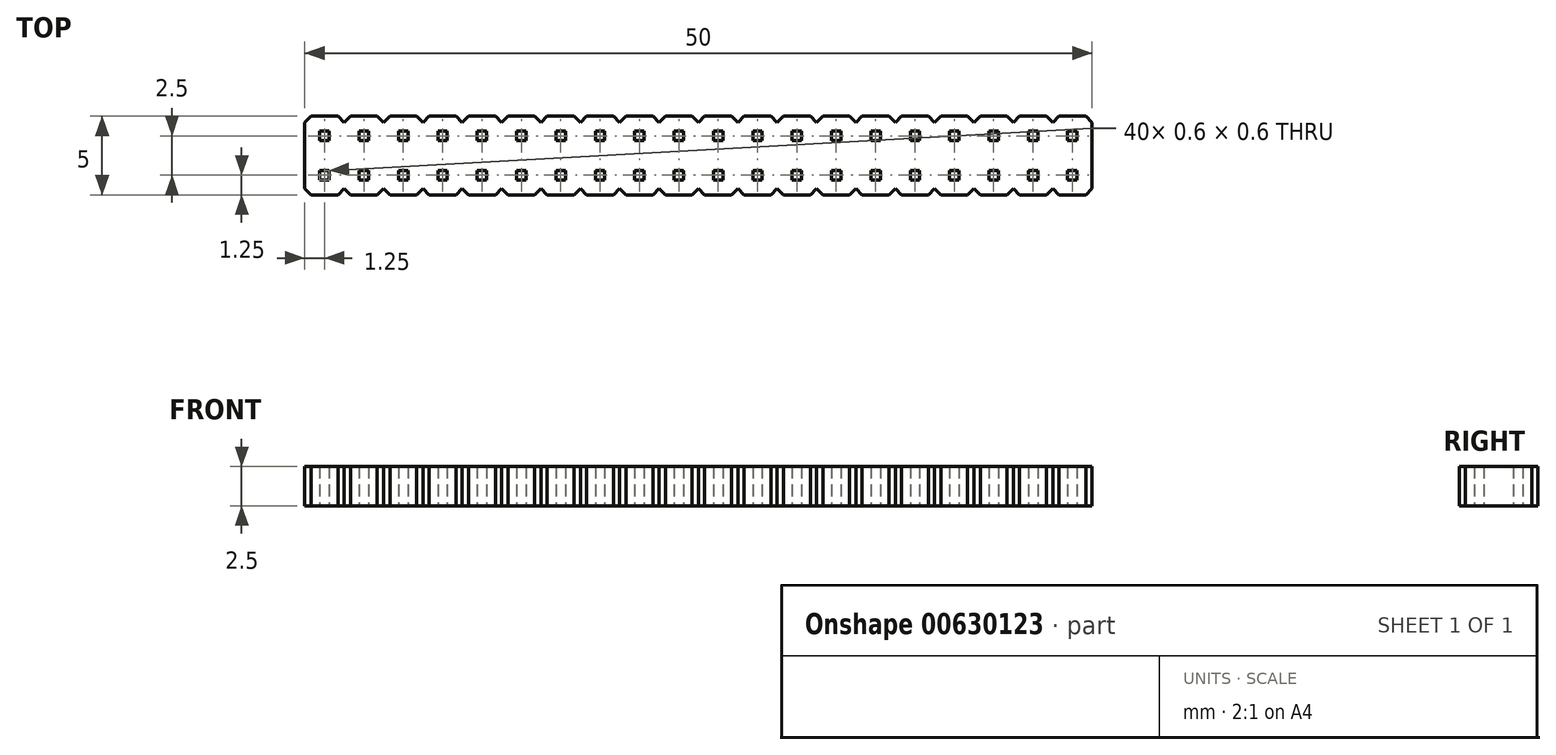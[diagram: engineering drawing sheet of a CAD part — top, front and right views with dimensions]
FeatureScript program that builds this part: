
annotation { "Feature Type Name" : "Feature", "Feature Type Description" : "" }
export const myFeature = defineFeature(function(context is Context, id is Id, definition is map)
    precondition{}
    {
        {
            var Q0;
            Q0=qCreatedBy(makeId("Top.planeOp"),FACE);
            var sketch = newSketch(context, id + "F0", { "sketchPlane" : qUnion([Q0])});
            skLineSegment(sketch, "E0.bottom", {"start": v(0.4, 0) * mm, "end": v(2.1, 0) * mm});
            skLineSegment(sketch, "E0.top", {"start": v(0.4, 5) * mm, "end": v(2.1, 5) * mm});
            skLineSegment(sketch, "E0.left", {"start": v(0, 0.4) * mm, "end": v(0, 4.6) * mm});
            skLineSegment(sketch, "E0.right", {"start": v(50, 0.4) * mm, "end": v(50, 4.6) * mm});
            skLineSegment(sketch, "E1", {"start": v(25, 5) * mm, "end": v(25, 0) * mm, "construction": true});
            skLineSegment(sketch, "E2", {"start": v(0, 2.5) * mm, "end": v(50, 2.5) * mm, "construction": true});
            skLineSegment(sketch, "E3.bottom", {"start": v(0.95, 4.05) * mm, "end": v(1.55, 4.05) * mm});
            skLineSegment(sketch, "E3.top", {"start": v(0.95, 3.45) * mm, "end": v(1.55, 3.45) * mm});
            skLineSegment(sketch, "E3.left", {"start": v(0.95, 4.05) * mm, "end": v(0.95, 3.45) * mm});
            skLineSegment(sketch, "E3.right", {"start": v(1.55, 4.05) * mm, "end": v(1.55, 3.45) * mm});
            skLineSegment(sketch, "E4", {"start": v(0, 4.6) * mm, "end": v(0.4, 5) * mm});
            skLineSegment(sketch, "E5", {"start": v(2.5, 5) * mm, "end": v(2.5, 2.5) * mm, "construction": true});
            skLineSegment(sketch, "E6", {"start": v(2.1, 5) * mm, "end": v(2.5, 4.6) * mm});
            skLineSegment(sketch, "E7.1.0.0", {"start": v(3.45, 3.45) * mm, "end": v(4.05, 3.45) * mm});
            skLineSegment(sketch, "E7.1.0.1", {"start": v(3.45, 4.05) * mm, "end": v(3.45, 3.45) * mm});
            skLineSegment(sketch, "E7.1.0.2", {"start": v(4.05, 4.05) * mm, "end": v(4.05, 3.45) * mm});
            skLineSegment(sketch, "E7.1.0.3", {"start": v(3.45, 4.05) * mm, "end": v(4.05, 4.05) * mm});
            skLineSegment(sketch, "E7.1.0.4", {"start": v(2.5, 4.6) * mm, "end": v(2.9, 5) * mm});
            skLineSegment(sketch, "E7.1.0.5", {"start": v(4.6, 5) * mm, "end": v(5, 4.6) * mm});
            skLineSegment(sketch, "E7.2.0.0", {"start": v(5.95, 3.45) * mm, "end": v(6.55, 3.45) * mm});
            skLineSegment(sketch, "E7.2.0.1", {"start": v(5.95, 4.05) * mm, "end": v(5.95, 3.45) * mm});
            skLineSegment(sketch, "E7.2.0.2", {"start": v(6.55, 4.05) * mm, "end": v(6.55, 3.45) * mm});
            skLineSegment(sketch, "E7.2.0.3", {"start": v(5.95, 4.05) * mm, "end": v(6.55, 4.05) * mm});
            skLineSegment(sketch, "E7.2.0.4", {"start": v(5, 4.6) * mm, "end": v(5.4, 5) * mm});
            skLineSegment(sketch, "E7.2.0.5", {"start": v(7.1, 5) * mm, "end": v(7.5, 4.6) * mm});
            skLineSegment(sketch, "E7.3.0.0", {"start": v(8.45, 3.45) * mm, "end": v(9.05, 3.45) * mm});
            skLineSegment(sketch, "E7.3.0.1", {"start": v(8.45, 4.05) * mm, "end": v(8.45, 3.45) * mm});
            skLineSegment(sketch, "E7.3.0.2", {"start": v(9.05, 4.05) * mm, "end": v(9.05, 3.45) * mm});
            skLineSegment(sketch, "E7.3.0.3", {"start": v(8.45, 4.05) * mm, "end": v(9.05, 4.05) * mm});
            skLineSegment(sketch, "E7.3.0.4", {"start": v(7.5, 4.6) * mm, "end": v(7.9, 5) * mm});
            skLineSegment(sketch, "E7.3.0.5", {"start": v(9.6, 5) * mm, "end": v(10, 4.6) * mm});
            skLineSegment(sketch, "E7.4.0.0", {"start": v(10.95, 3.45) * mm, "end": v(11.55, 3.45) * mm});
            skLineSegment(sketch, "E7.4.0.1", {"start": v(10.95, 4.05) * mm, "end": v(10.95, 3.45) * mm});
            skLineSegment(sketch, "E7.4.0.2", {"start": v(11.55, 4.05) * mm, "end": v(11.55, 3.45) * mm});
            skLineSegment(sketch, "E7.4.0.3", {"start": v(10.95, 4.05) * mm, "end": v(11.55, 4.05) * mm});
            skLineSegment(sketch, "E7.4.0.4", {"start": v(10, 4.6) * mm, "end": v(10.4, 5) * mm});
            skLineSegment(sketch, "E7.4.0.5", {"start": v(12.1, 5) * mm, "end": v(12.5, 4.6) * mm});
            skLineSegment(sketch, "E7.5.0.0", {"start": v(13.45, 3.45) * mm, "end": v(14.05, 3.45) * mm});
            skLineSegment(sketch, "E7.5.0.1", {"start": v(13.45, 4.05) * mm, "end": v(13.45, 3.45) * mm});
            skLineSegment(sketch, "E7.5.0.2", {"start": v(14.05, 4.05) * mm, "end": v(14.05, 3.45) * mm});
            skLineSegment(sketch, "E7.5.0.3", {"start": v(13.45, 4.05) * mm, "end": v(14.05, 4.05) * mm});
            skLineSegment(sketch, "E7.5.0.4", {"start": v(12.5, 4.6) * mm, "end": v(12.9, 5) * mm});
            skLineSegment(sketch, "E7.5.0.5", {"start": v(14.6, 5) * mm, "end": v(15, 4.6) * mm});
            skLineSegment(sketch, "E7.6.0.0", {"start": v(15.95, 3.45) * mm, "end": v(16.55, 3.45) * mm});
            skLineSegment(sketch, "E7.6.0.1", {"start": v(15.95, 4.05) * mm, "end": v(15.95, 3.45) * mm});
            skLineSegment(sketch, "E7.6.0.2", {"start": v(16.55, 4.05) * mm, "end": v(16.55, 3.45) * mm});
            skLineSegment(sketch, "E7.6.0.3", {"start": v(15.95, 4.05) * mm, "end": v(16.55, 4.05) * mm});
            skLineSegment(sketch, "E7.6.0.4", {"start": v(15, 4.6) * mm, "end": v(15.4, 5) * mm});
            skLineSegment(sketch, "E7.6.0.5", {"start": v(17.1, 5) * mm, "end": v(17.5, 4.6) * mm});
            skLineSegment(sketch, "E7.7.0.0", {"start": v(18.45, 3.45) * mm, "end": v(19.05, 3.45) * mm});
            skLineSegment(sketch, "E7.7.0.1", {"start": v(18.45, 4.05) * mm, "end": v(18.45, 3.45) * mm});
            skLineSegment(sketch, "E7.7.0.2", {"start": v(19.05, 4.05) * mm, "end": v(19.05, 3.45) * mm});
            skLineSegment(sketch, "E7.7.0.3", {"start": v(18.45, 4.05) * mm, "end": v(19.05, 4.05) * mm});
            skLineSegment(sketch, "E7.7.0.4", {"start": v(17.5, 4.6) * mm, "end": v(17.9, 5) * mm});
            skLineSegment(sketch, "E7.7.0.5", {"start": v(19.6, 5) * mm, "end": v(20, 4.6) * mm});
            skLineSegment(sketch, "E7.8.0.0", {"start": v(20.95, 3.45) * mm, "end": v(21.55, 3.45) * mm});
            skLineSegment(sketch, "E7.8.0.1", {"start": v(20.95, 4.05) * mm, "end": v(20.95, 3.45) * mm});
            skLineSegment(sketch, "E7.8.0.2", {"start": v(21.55, 4.05) * mm, "end": v(21.55, 3.45) * mm});
            skLineSegment(sketch, "E7.8.0.3", {"start": v(20.95, 4.05) * mm, "end": v(21.55, 4.05) * mm});
            skLineSegment(sketch, "E7.8.0.4", {"start": v(20, 4.6) * mm, "end": v(20.4, 5) * mm});
            skLineSegment(sketch, "E7.8.0.5", {"start": v(22.1, 5) * mm, "end": v(22.5, 4.6) * mm});
            skLineSegment(sketch, "E7.9.0.0", {"start": v(23.45, 3.45) * mm, "end": v(24.05, 3.45) * mm});
            skLineSegment(sketch, "E7.9.0.1", {"start": v(23.45, 4.05) * mm, "end": v(23.45, 3.45) * mm});
            skLineSegment(sketch, "E7.9.0.2", {"start": v(24.05, 4.05) * mm, "end": v(24.05, 3.45) * mm});
            skLineSegment(sketch, "E7.9.0.3", {"start": v(23.45, 4.05) * mm, "end": v(24.05, 4.05) * mm});
            skLineSegment(sketch, "E7.9.0.4", {"start": v(22.5, 4.6) * mm, "end": v(22.9, 5) * mm});
            skLineSegment(sketch, "E7.9.0.5", {"start": v(24.6, 5) * mm, "end": v(25, 4.6) * mm});
            skLineSegment(sketch, "E7.direction1", {"start": v(0.95, 3.45) * mm, "end": v(3.45, 3.45) * mm, "construction": true});
            skLineSegment(sketch, "E8.MirrorCS", {"start": v(23.45, 0.95) * mm, "end": v(24.05, 0.95) * mm});
            skLineSegment(sketch, "E9.MirrorCS", {"start": v(20.95, 1.55) * mm, "end": v(21.55, 1.55) * mm});
            skLineSegment(sketch, "E10.MirrorCS", {"start": v(23.45, 1.55) * mm, "end": v(24.05, 1.55) * mm});
            skLineSegment(sketch, "E11.MirrorCS", {"start": v(20.95, 0.95) * mm, "end": v(21.55, 0.95) * mm});
            skLineSegment(sketch, "E12.MirrorCS", {"start": v(0.95, 1.55) * mm, "end": v(1.55, 1.55) * mm});
            skLineSegment(sketch, "E13.MirrorCS", {"start": v(10.95, 0.95) * mm, "end": v(11.55, 0.95) * mm});
            skLineSegment(sketch, "E14.MirrorCS", {"start": v(18.45, 0.95) * mm, "end": v(18.45, 1.55) * mm});
            skLineSegment(sketch, "E15.MirrorCS", {"start": v(8.45, 1.55) * mm, "end": v(9.05, 1.55) * mm});
            skLineSegment(sketch, "E16.MirrorCS", {"start": v(21.55, 0.95) * mm, "end": v(21.55, 1.55) * mm});
            skLineSegment(sketch, "E17.MirrorCS", {"start": v(11.55, 0.95) * mm, "end": v(11.55, 1.55) * mm});
            skLineSegment(sketch, "E18.MirrorCS", {"start": v(18.45, 1.55) * mm, "end": v(19.05, 1.55) * mm});
            skLineSegment(sketch, "E19.MirrorCS", {"start": v(13.45, 0.95) * mm, "end": v(14.05, 0.95) * mm});
            skLineSegment(sketch, "E20.MirrorCS", {"start": v(20.95, 0.95) * mm, "end": v(20.95, 1.55) * mm});
            skLineSegment(sketch, "E21.MirrorCS", {"start": v(10.95, 0.95) * mm, "end": v(10.95, 1.55) * mm});
            skLineSegment(sketch, "E22.MirrorCS", {"start": v(3.45, 0.95) * mm, "end": v(4.05, 0.95) * mm});
            skLineSegment(sketch, "E23.MirrorCS", {"start": v(14.05, 0.95) * mm, "end": v(14.05, 1.55) * mm});
            skLineSegment(sketch, "E24.MirrorCS", {"start": v(1.55, 0.95) * mm, "end": v(1.55, 1.55) * mm});
            skLineSegment(sketch, "E25.MirrorCS", {"start": v(0.95, 0.95) * mm, "end": v(0.95, 1.55) * mm});
            skLineSegment(sketch, "E26.MirrorCS", {"start": v(0.95, 0.95) * mm, "end": v(1.55, 0.95) * mm});
            skLineSegment(sketch, "E27.MirrorCS", {"start": v(4.05, 0.95) * mm, "end": v(4.05, 1.55) * mm});
            skLineSegment(sketch, "E28.MirrorCS", {"start": v(3.45, 0.95) * mm, "end": v(3.45, 1.55) * mm});
            skLineSegment(sketch, "E29.MirrorCS", {"start": v(3.45, 1.55) * mm, "end": v(4.05, 1.55) * mm});
            skLineSegment(sketch, "E30.MirrorCS", {"start": v(13.45, 0.95) * mm, "end": v(13.45, 1.55) * mm});
            skLineSegment(sketch, "E31.MirrorCS", {"start": v(10.95, 1.55) * mm, "end": v(11.55, 1.55) * mm});
            skLineSegment(sketch, "E32.MirrorCS", {"start": v(24.05, 0.95) * mm, "end": v(24.05, 1.55) * mm});
            skLineSegment(sketch, "E33.MirrorCS", {"start": v(5.95, 0.95) * mm, "end": v(6.55, 0.95) * mm});
            skLineSegment(sketch, "E34.MirrorCS", {"start": v(13.45, 1.55) * mm, "end": v(14.05, 1.55) * mm});
            skLineSegment(sketch, "E35.MirrorCS", {"start": v(15.95, 0.95) * mm, "end": v(16.55, 0.95) * mm});
            skLineSegment(sketch, "E36.MirrorCS", {"start": v(23.45, 0.95) * mm, "end": v(23.45, 1.55) * mm});
            skLineSegment(sketch, "E37.MirrorCS", {"start": v(6.55, 0.95) * mm, "end": v(6.55, 1.55) * mm});
            skLineSegment(sketch, "E38.MirrorCS", {"start": v(8.45, 0.95) * mm, "end": v(9.05, 0.95) * mm});
            skLineSegment(sketch, "E39.MirrorCS", {"start": v(15.95, 0.95) * mm, "end": v(15.95, 1.55) * mm});
            skLineSegment(sketch, "E40.MirrorCS", {"start": v(18.45, 0.95) * mm, "end": v(19.05, 0.95) * mm});
            skLineSegment(sketch, "E41.MirrorCS", {"start": v(16.55, 0.95) * mm, "end": v(16.55, 1.55) * mm});
            skLineSegment(sketch, "E42.MirrorCS", {"start": v(15.95, 1.55) * mm, "end": v(16.55, 1.55) * mm});
            skLineSegment(sketch, "E43.MirrorCS", {"start": v(9.05, 0.95) * mm, "end": v(9.05, 1.55) * mm});
            skLineSegment(sketch, "E44.MirrorCS", {"start": v(5.95, 0.95) * mm, "end": v(5.95, 1.55) * mm});
            skLineSegment(sketch, "E45.MirrorCS", {"start": v(19.05, 0.95) * mm, "end": v(19.05, 1.55) * mm});
            skLineSegment(sketch, "E46.MirrorCS", {"start": v(8.45, 0.95) * mm, "end": v(8.45, 1.55) * mm});
            skLineSegment(sketch, "E47.MirrorCS", {"start": v(5.95, 1.55) * mm, "end": v(6.55, 1.55) * mm});
            skLineSegment(sketch, "E48.MirrorCS", {"start": v(0.95, 1.55) * mm, "end": v(3.45, 1.55) * mm, "construction": true});
            skLineSegment(sketch, "E49.MirrorCS", {"start": v(0, 0.4) * mm, "end": v(0.4, 0) * mm});
            skLineSegment(sketch, "E50.MirrorCS", {"start": v(2.1, 0) * mm, "end": v(2.5, 0.4) * mm});
            skLineSegment(sketch, "E51.MirrorCS", {"start": v(2.5, 0.4) * mm, "end": v(2.9, 0) * mm});
            skLineSegment(sketch, "E52.MirrorCS", {"start": v(4.6, 0) * mm, "end": v(5, 0.4) * mm});
            skLineSegment(sketch, "E53.MirrorCS", {"start": v(5, 0.4) * mm, "end": v(5.4, 0) * mm});
            skLineSegment(sketch, "E54.MirrorCS", {"start": v(7.1, 0) * mm, "end": v(7.5, 0.4) * mm});
            skLineSegment(sketch, "E55.MirrorCS", {"start": v(7.5, 0.4) * mm, "end": v(7.9, 0) * mm});
            skLineSegment(sketch, "E56.MirrorCS", {"start": v(9.6, 0) * mm, "end": v(10, 0.4) * mm});
            skLineSegment(sketch, "E57.MirrorCS", {"start": v(10, 0.4) * mm, "end": v(10.4, 0) * mm});
            skLineSegment(sketch, "E58.MirrorCS", {"start": v(12.1, 0) * mm, "end": v(12.5, 0.4) * mm});
            skLineSegment(sketch, "E59.MirrorCS", {"start": v(12.5, 0.4) * mm, "end": v(12.9, 0) * mm});
            skLineSegment(sketch, "E60.MirrorCS", {"start": v(14.6, 0) * mm, "end": v(15, 0.4) * mm});
            skLineSegment(sketch, "E61.MirrorCS", {"start": v(15, 0.4) * mm, "end": v(15.4, 0) * mm});
            skLineSegment(sketch, "E62.MirrorCS", {"start": v(17.1, 0) * mm, "end": v(17.5, 0.4) * mm});
            skLineSegment(sketch, "E63.MirrorCS", {"start": v(17.5, 0.4) * mm, "end": v(17.9, 0) * mm});
            skLineSegment(sketch, "E64.MirrorCS", {"start": v(19.6, 0) * mm, "end": v(20, 0.4) * mm});
            skLineSegment(sketch, "E65.MirrorCS", {"start": v(20, 0.4) * mm, "end": v(20.4, 0) * mm});
            skLineSegment(sketch, "E66.MirrorCS", {"start": v(22.1, 0) * mm, "end": v(22.5, 0.4) * mm});
            skLineSegment(sketch, "E67.MirrorCS", {"start": v(22.5, 0.4) * mm, "end": v(22.9, 0) * mm});
            skLineSegment(sketch, "E68.MirrorCS", {"start": v(24.6, 0) * mm, "end": v(25, 0.4) * mm});
            skLineSegment(sketch, "E69.MirrorCS", {"start": v(49.05, 1.55) * mm, "end": v(48.45, 1.55) * mm});
            skLineSegment(sketch, "E70.MirrorCS", {"start": v(49.05, 3.45) * mm, "end": v(48.45, 3.45) * mm});
            skLineSegment(sketch, "E71.MirrorCS", {"start": v(41.55, 0.95) * mm, "end": v(40.95, 0.95) * mm});
            skLineSegment(sketch, "E72.MirrorCS", {"start": v(39.05, 4.05) * mm, "end": v(38.45, 4.05) * mm});
            skLineSegment(sketch, "E73.MirrorCS", {"start": v(31.55, 4.05) * mm, "end": v(31.55, 3.45) * mm});
            skLineSegment(sketch, "E74.MirrorCS", {"start": v(46.55, 0.95) * mm, "end": v(45.95, 0.95) * mm});
            skLineSegment(sketch, "E75.MirrorCS", {"start": v(44.05, 3.45) * mm, "end": v(43.45, 3.45) * mm});
            skLineSegment(sketch, "E76.MirrorCS", {"start": v(35.95, 0.95) * mm, "end": v(35.95, 1.55) * mm});
            skLineSegment(sketch, "E77.MirrorCS", {"start": v(49.05, 3.45) * mm, "end": v(46.55, 3.45) * mm, "construction": true});
            skLineSegment(sketch, "E78.MirrorCS", {"start": v(30.95, 4.05) * mm, "end": v(30.95, 3.45) * mm});
            skLineSegment(sketch, "E79.MirrorCS", {"start": v(34.05, 0.95) * mm, "end": v(34.05, 1.55) * mm});
            skLineSegment(sketch, "E80.MirrorCS", {"start": v(49.05, 1.55) * mm, "end": v(46.55, 1.55) * mm, "construction": true});
            skLineSegment(sketch, "E81.MirrorCS", {"start": v(25.95, 0.95) * mm, "end": v(25.95, 1.55) * mm});
            skLineSegment(sketch, "E82.MirrorCS", {"start": v(28.45, 0.95) * mm, "end": v(28.45, 1.55) * mm});
            skLineSegment(sketch, "E83.MirrorCS", {"start": v(41.55, 4.05) * mm, "end": v(40.95, 4.05) * mm});
            skLineSegment(sketch, "E84.MirrorCS", {"start": v(43.45, 0.95) * mm, "end": v(43.45, 1.55) * mm});
            skLineSegment(sketch, "E85.MirrorCS", {"start": v(38.45, 4.05) * mm, "end": v(38.45, 3.45) * mm});
            skLineSegment(sketch, "E86.MirrorCS", {"start": v(31.55, 3.45) * mm, "end": v(30.95, 3.45) * mm});
            skLineSegment(sketch, "E87.MirrorCS", {"start": v(31.55, 1.55) * mm, "end": v(30.95, 1.55) * mm});
            skLineSegment(sketch, "E88.MirrorCS", {"start": v(34.05, 4.05) * mm, "end": v(33.45, 4.05) * mm});
            skLineSegment(sketch, "E89.MirrorCS", {"start": v(39.05, 0.95) * mm, "end": v(39.05, 1.55) * mm});
            skLineSegment(sketch, "E90.MirrorCS", {"start": v(34.05, 4.05) * mm, "end": v(34.05, 3.45) * mm});
            skLineSegment(sketch, "E91.MirrorCS", {"start": v(39.05, 4.05) * mm, "end": v(39.05, 3.45) * mm});
            skLineSegment(sketch, "E92.MirrorCS", {"start": v(44.05, 0.95) * mm, "end": v(43.45, 0.95) * mm});
            skLineSegment(sketch, "E93.MirrorCS", {"start": v(26.55, 4.05) * mm, "end": v(25.95, 4.05) * mm});
            skLineSegment(sketch, "E94.MirrorCS", {"start": v(29.05, 0.95) * mm, "end": v(29.05, 1.55) * mm});
            skLineSegment(sketch, "E95.MirrorCS", {"start": v(46.55, 4.05) * mm, "end": v(45.95, 4.05) * mm});
            skLineSegment(sketch, "E96.MirrorCS", {"start": v(33.45, 4.05) * mm, "end": v(33.45, 3.45) * mm});
            skLineSegment(sketch, "E97.MirrorCS", {"start": v(26.55, 3.45) * mm, "end": v(25.95, 3.45) * mm});
            skLineSegment(sketch, "E98.MirrorCS", {"start": v(38.45, 0.95) * mm, "end": v(38.45, 1.55) * mm});
            skLineSegment(sketch, "E99.MirrorCS", {"start": v(41.55, 1.55) * mm, "end": v(40.95, 1.55) * mm});
            skLineSegment(sketch, "E100.MirrorCS", {"start": v(39.05, 1.55) * mm, "end": v(38.45, 1.55) * mm});
            skLineSegment(sketch, "E101.MirrorCS", {"start": v(44.05, 1.55) * mm, "end": v(43.45, 1.55) * mm});
            skLineSegment(sketch, "E102.MirrorCS", {"start": v(40.95, 4.05) * mm, "end": v(40.95, 3.45) * mm});
            skLineSegment(sketch, "E103.MirrorCS", {"start": v(34.05, 3.45) * mm, "end": v(33.45, 3.45) * mm});
            skLineSegment(sketch, "E104.MirrorCS", {"start": v(26.55, 0.95) * mm, "end": v(26.55, 1.55) * mm});
            skLineSegment(sketch, "E105.MirrorCS", {"start": v(26.55, 4.05) * mm, "end": v(26.55, 3.45) * mm});
            skLineSegment(sketch, "E106.MirrorCS", {"start": v(44.05, 4.05) * mm, "end": v(44.05, 3.45) * mm});
            skLineSegment(sketch, "E107.MirrorCS", {"start": v(48.45, 0.95) * mm, "end": v(48.45, 1.55) * mm});
            skLineSegment(sketch, "E108.MirrorCS", {"start": v(26.55, 0.95) * mm, "end": v(25.95, 0.95) * mm});
            skLineSegment(sketch, "E109.MirrorCS", {"start": v(31.55, 4.05) * mm, "end": v(30.95, 4.05) * mm});
            skLineSegment(sketch, "E110.MirrorCS", {"start": v(36.55, 1.55) * mm, "end": v(35.95, 1.55) * mm});
            skLineSegment(sketch, "E111.MirrorCS", {"start": v(31.55, 0.95) * mm, "end": v(30.95, 0.95) * mm});
            skLineSegment(sketch, "E112.MirrorCS", {"start": v(36.55, 0.95) * mm, "end": v(36.55, 1.55) * mm});
            skLineSegment(sketch, "E113.MirrorCS", {"start": v(43.45, 4.05) * mm, "end": v(43.45, 3.45) * mm});
            skLineSegment(sketch, "E114.MirrorCS", {"start": v(49.05, 0.95) * mm, "end": v(49.05, 1.55) * mm});
            skLineSegment(sketch, "E115.MirrorCS", {"start": v(29.05, 1.55) * mm, "end": v(28.45, 1.55) * mm});
            skLineSegment(sketch, "E116.MirrorCS", {"start": v(36.55, 0.95) * mm, "end": v(35.95, 0.95) * mm});
            skLineSegment(sketch, "E117.MirrorCS", {"start": v(25.95, 4.05) * mm, "end": v(25.95, 3.45) * mm});
            skLineSegment(sketch, "E118.MirrorCS", {"start": v(36.55, 3.45) * mm, "end": v(35.95, 3.45) * mm});
            skLineSegment(sketch, "E119.MirrorCS", {"start": v(39.05, 3.45) * mm, "end": v(38.45, 3.45) * mm});
            skLineSegment(sketch, "E120.MirrorCS", {"start": v(33.45, 0.95) * mm, "end": v(33.45, 1.55) * mm});
            skLineSegment(sketch, "E121.MirrorCS", {"start": v(34.05, 0.95) * mm, "end": v(33.45, 0.95) * mm});
            skLineSegment(sketch, "E122.MirrorCS", {"start": v(46.55, 3.45) * mm, "end": v(45.95, 3.45) * mm});
            skLineSegment(sketch, "E123.MirrorCS", {"start": v(46.55, 4.05) * mm, "end": v(46.55, 3.45) * mm});
            skLineSegment(sketch, "E124.MirrorCS", {"start": v(45.95, 4.05) * mm, "end": v(45.95, 3.45) * mm});
            skLineSegment(sketch, "E125.MirrorCS", {"start": v(49.05, 0.95) * mm, "end": v(48.45, 0.95) * mm});
            skLineSegment(sketch, "E126.MirrorCS", {"start": v(44.05, 4.05) * mm, "end": v(43.45, 4.05) * mm});
            skLineSegment(sketch, "E127.MirrorCS", {"start": v(26.55, 1.55) * mm, "end": v(25.95, 1.55) * mm});
            skLineSegment(sketch, "E128.MirrorCS", {"start": v(36.55, 4.05) * mm, "end": v(36.55, 3.45) * mm});
            skLineSegment(sketch, "E129.MirrorCS", {"start": v(34.05, 1.55) * mm, "end": v(33.45, 1.55) * mm});
            skLineSegment(sketch, "E130.MirrorCS", {"start": v(35.95, 4.05) * mm, "end": v(35.95, 3.45) * mm});
            skLineSegment(sketch, "E131.MirrorCS", {"start": v(29.05, 3.45) * mm, "end": v(28.45, 3.45) * mm});
            skLineSegment(sketch, "E132.MirrorCS", {"start": v(45.95, 0.95) * mm, "end": v(45.95, 1.55) * mm});
            skLineSegment(sketch, "E133.MirrorCS", {"start": v(29.05, 0.95) * mm, "end": v(28.45, 0.95) * mm});
            skLineSegment(sketch, "E134.MirrorCS", {"start": v(40.95, 0.95) * mm, "end": v(40.95, 1.55) * mm});
            skLineSegment(sketch, "E135.MirrorCS", {"start": v(36.55, 4.05) * mm, "end": v(35.95, 4.05) * mm});
            skLineSegment(sketch, "E136.MirrorCS", {"start": v(29.05, 4.05) * mm, "end": v(29.05, 3.45) * mm});
            skLineSegment(sketch, "E137.MirrorCS", {"start": v(44.05, 0.95) * mm, "end": v(44.05, 1.55) * mm});
            skLineSegment(sketch, "E138.MirrorCS", {"start": v(46.55, 0.95) * mm, "end": v(46.55, 1.55) * mm});
            skLineSegment(sketch, "E139.MirrorCS", {"start": v(28.45, 4.05) * mm, "end": v(28.45, 3.45) * mm});
            skLineSegment(sketch, "E140.MirrorCS", {"start": v(46.55, 1.55) * mm, "end": v(45.95, 1.55) * mm});
            skLineSegment(sketch, "E141.MirrorCS", {"start": v(31.55, 0.95) * mm, "end": v(31.55, 1.55) * mm});
            skLineSegment(sketch, "E142.MirrorCS", {"start": v(41.55, 3.45) * mm, "end": v(40.95, 3.45) * mm});
            skLineSegment(sketch, "E143.MirrorCS", {"start": v(30.95, 0.95) * mm, "end": v(30.95, 1.55) * mm});
            skLineSegment(sketch, "E144.MirrorCS", {"start": v(49.05, 4.05) * mm, "end": v(49.05, 3.45) * mm});
            skLineSegment(sketch, "E145.MirrorCS", {"start": v(48.45, 4.05) * mm, "end": v(48.45, 3.45) * mm});
            skLineSegment(sketch, "E146.MirrorCS", {"start": v(39.05, 0.95) * mm, "end": v(38.45, 0.95) * mm});
            skLineSegment(sketch, "E147.MirrorCS", {"start": v(41.55, 0.95) * mm, "end": v(41.55, 1.55) * mm});
            skLineSegment(sketch, "E148.MirrorCS", {"start": v(49.05, 4.05) * mm, "end": v(48.45, 4.05) * mm});
            skLineSegment(sketch, "E149.MirrorCS", {"start": v(41.55, 4.05) * mm, "end": v(41.55, 3.45) * mm});
            skLineSegment(sketch, "E150.MirrorCS", {"start": v(29.05, 4.05) * mm, "end": v(28.45, 4.05) * mm});
            skLineSegment(sketch, "E151.MirrorCS", {"start": v(50, 4.6) * mm, "end": v(49.6, 5) * mm});
            skLineSegment(sketch, "E152.MirrorCS", {"start": v(50, 0.4) * mm, "end": v(49.6, 0) * mm});
            skLineSegment(sketch, "E153.MirrorCS", {"start": v(47.9, 5) * mm, "end": v(47.5, 4.6) * mm});
            skLineSegment(sketch, "E154.MirrorCS", {"start": v(47.9, 0) * mm, "end": v(47.5, 0.4) * mm});
            skLineSegment(sketch, "E155.MirrorCS", {"start": v(47.5, 4.6) * mm, "end": v(47.1, 5) * mm});
            skLineSegment(sketch, "E156.MirrorCS", {"start": v(47.5, 0.4) * mm, "end": v(47.1, 0) * mm});
            skLineSegment(sketch, "E157.MirrorCS", {"start": v(45.4, 0) * mm, "end": v(45, 0.4) * mm});
            skLineSegment(sketch, "E158.MirrorCS", {"start": v(45.4, 5) * mm, "end": v(45, 4.6) * mm});
            skLineSegment(sketch, "E159.MirrorCS", {"start": v(45, 4.6) * mm, "end": v(44.6, 5) * mm});
            skLineSegment(sketch, "E160.MirrorCS", {"start": v(45, 0.4) * mm, "end": v(44.6, 0) * mm});
            skLineSegment(sketch, "E161.MirrorCS", {"start": v(42.9, 5) * mm, "end": v(42.5, 4.6) * mm});
            skLineSegment(sketch, "E162.MirrorCS", {"start": v(42.9, 0) * mm, "end": v(42.5, 0.4) * mm});
            skLineSegment(sketch, "E163.MirrorCS", {"start": v(42.5, 4.6) * mm, "end": v(42.1, 5) * mm});
            skLineSegment(sketch, "E164.MirrorCS", {"start": v(42.5, 0.4) * mm, "end": v(42.1, 0) * mm});
            skLineSegment(sketch, "E165.MirrorCS", {"start": v(40.4, 5) * mm, "end": v(40, 4.6) * mm});
            skLineSegment(sketch, "E166.MirrorCS", {"start": v(40.4, 0) * mm, "end": v(40, 0.4) * mm});
            skLineSegment(sketch, "E167.MirrorCS", {"start": v(40, 4.6) * mm, "end": v(39.6, 5) * mm});
            skLineSegment(sketch, "E168.MirrorCS", {"start": v(40, 0.4) * mm, "end": v(39.6, 0) * mm});
            skLineSegment(sketch, "E169.MirrorCS", {"start": v(37.9, 5) * mm, "end": v(37.5, 4.6) * mm});
            skLineSegment(sketch, "E170.MirrorCS", {"start": v(37.9, 0) * mm, "end": v(37.5, 0.4) * mm});
            skLineSegment(sketch, "E171.MirrorCS", {"start": v(37.5, 4.6) * mm, "end": v(37.1, 5) * mm});
            skLineSegment(sketch, "E172.MirrorCS", {"start": v(37.5, 0.4) * mm, "end": v(37.1, 0) * mm});
            skLineSegment(sketch, "E173.MirrorCS", {"start": v(25.4, 5) * mm, "end": v(25, 4.6) * mm});
            skLineSegment(sketch, "E174.MirrorCS", {"start": v(25.4, 0) * mm, "end": v(25, 0.4) * mm});
            skLineSegment(sketch, "E175.MirrorCS", {"start": v(27.5, 0.4) * mm, "end": v(27.1, 0) * mm});
            skLineSegment(sketch, "E176.MirrorCS", {"start": v(27.5, 4.6) * mm, "end": v(27.1, 5) * mm});
            skLineSegment(sketch, "E177.MirrorCS", {"start": v(27.9, 5) * mm, "end": v(27.5, 4.6) * mm});
            skLineSegment(sketch, "E178.MirrorCS", {"start": v(27.9, 0) * mm, "end": v(27.5, 0.4) * mm});
            skLineSegment(sketch, "E179.MirrorCS", {"start": v(30, 0.4) * mm, "end": v(29.6, 0) * mm});
            skLineSegment(sketch, "E180.MirrorCS", {"start": v(30, 4.6) * mm, "end": v(29.6, 5) * mm});
            skLineSegment(sketch, "E181.MirrorCS", {"start": v(30.4, 5) * mm, "end": v(30, 4.6) * mm});
            skLineSegment(sketch, "E182.MirrorCS", {"start": v(30.4, 0) * mm, "end": v(30, 0.4) * mm});
            skLineSegment(sketch, "E183.MirrorCS", {"start": v(32.5, 4.6) * mm, "end": v(32.1, 5) * mm});
            skLineSegment(sketch, "E184.MirrorCS", {"start": v(32.5, 0.4) * mm, "end": v(32.1, 0) * mm});
            skLineSegment(sketch, "E185.MirrorCS", {"start": v(32.9, 0) * mm, "end": v(32.5, 0.4) * mm});
            skLineSegment(sketch, "E186.MirrorCS", {"start": v(32.9, 5) * mm, "end": v(32.5, 4.6) * mm});
            skLineSegment(sketch, "E187.MirrorCS", {"start": v(35, 4.6) * mm, "end": v(34.6, 5) * mm});
            skLineSegment(sketch, "E188.MirrorCS", {"start": v(35, 0.4) * mm, "end": v(34.6, 0) * mm});
            skLineSegment(sketch, "E189.MirrorCS", {"start": v(35.4, 5) * mm, "end": v(35, 4.6) * mm});
            skLineSegment(sketch, "E190.MirrorCS", {"start": v(35.4, 0) * mm, "end": v(35, 0.4) * mm});
            skPoint(sketch, "E191.orphan", {"position": v(0, 5) * mm});
            skLineSegment(sketch, "E192.trimOffspring", {"start": v(2.9, 5) * mm, "end": v(4.6, 5) * mm});
            skLineSegment(sketch, "E193.trimOffspring", {"start": v(5.4, 5) * mm, "end": v(7.1, 5) * mm});
            skLineSegment(sketch, "E194.trimOffspring", {"start": v(7.9, 5) * mm, "end": v(9.6, 5) * mm});
            skLineSegment(sketch, "E195.trimOffspring", {"start": v(10.4, 5) * mm, "end": v(12.1, 5) * mm});
            skLineSegment(sketch, "E196.trimOffspring", {"start": v(12.9, 5) * mm, "end": v(14.6, 5) * mm});
            skLineSegment(sketch, "E197.trimOffspring", {"start": v(15.4, 5) * mm, "end": v(17.1, 5) * mm});
            skLineSegment(sketch, "E198.trimOffspring", {"start": v(17.9, 5) * mm, "end": v(19.6, 5) * mm});
            skLineSegment(sketch, "E199.trimOffspring", {"start": v(20.4, 5) * mm, "end": v(22.1, 5) * mm});
            skLineSegment(sketch, "E200.trimOffspring", {"start": v(22.9, 5) * mm, "end": v(24.6, 5) * mm});
            skLineSegment(sketch, "E201.trimOffspring", {"start": v(25.4, 5) * mm, "end": v(27.1, 5) * mm});
            skLineSegment(sketch, "E202.trimOffspring", {"start": v(27.9, 5) * mm, "end": v(29.6, 5) * mm});
            skLineSegment(sketch, "E203.trimOffspring", {"start": v(30.4, 5) * mm, "end": v(32.1, 5) * mm});
            skLineSegment(sketch, "E204.trimOffspring", {"start": v(32.9, 5) * mm, "end": v(34.6, 5) * mm});
            skLineSegment(sketch, "E205.trimOffspring", {"start": v(35.4, 5) * mm, "end": v(37.1, 5) * mm});
            skLineSegment(sketch, "E206.trimOffspring", {"start": v(37.9, 5) * mm, "end": v(39.6, 5) * mm});
            skLineSegment(sketch, "E207.trimOffspring", {"start": v(40.4, 5) * mm, "end": v(42.1, 5) * mm});
            skLineSegment(sketch, "E208.trimOffspring", {"start": v(42.9, 5) * mm, "end": v(44.6, 5) * mm});
            skLineSegment(sketch, "E209.trimOffspring", {"start": v(45.4, 5) * mm, "end": v(47.1, 5) * mm});
            skLineSegment(sketch, "E210.trimOffspring", {"start": v(47.9, 5) * mm, "end": v(49.6, 5) * mm});
            skPoint(sketch, "E211.orphan", {"position": v(50, 5) * mm});
            skPoint(sketch, "E212.orphan", {"position": v(50, 0) * mm});
            skLineSegment(sketch, "E213.trimOffspring", {"start": v(47.9, 0) * mm, "end": v(49.6, 0) * mm});
            skLineSegment(sketch, "E214.trimOffspring", {"start": v(45.4, 0) * mm, "end": v(47.1, 0) * mm});
            skLineSegment(sketch, "E215.trimOffspring", {"start": v(42.9, 0) * mm, "end": v(44.6, 0) * mm});
            skLineSegment(sketch, "E216.trimOffspring", {"start": v(40.4, 0) * mm, "end": v(42.1, 0) * mm});
            skLineSegment(sketch, "E217.trimOffspring", {"start": v(37.9, 0) * mm, "end": v(39.6, 0) * mm});
            skLineSegment(sketch, "E218.trimOffspring", {"start": v(35.4, 0) * mm, "end": v(37.1, 0) * mm});
            skLineSegment(sketch, "E219.trimOffspring", {"start": v(32.9, 0) * mm, "end": v(34.6, 0) * mm});
            skLineSegment(sketch, "E220.trimOffspring", {"start": v(30.4, 0) * mm, "end": v(32.1, 0) * mm});
            skLineSegment(sketch, "E221.trimOffspring", {"start": v(27.9, 0) * mm, "end": v(29.6, 0) * mm});
            skLineSegment(sketch, "E222.trimOffspring", {"start": v(25.4, 0) * mm, "end": v(27.1, 0) * mm});
            skLineSegment(sketch, "E223.trimOffspring", {"start": v(22.9, 0) * mm, "end": v(24.6, 0) * mm});
            skLineSegment(sketch, "E224.trimOffspring", {"start": v(20.4, 0) * mm, "end": v(22.1, 0) * mm});
            skLineSegment(sketch, "E225.trimOffspring", {"start": v(17.9, 0) * mm, "end": v(19.6, 0) * mm});
            skLineSegment(sketch, "E226.trimOffspring", {"start": v(15.4, 0) * mm, "end": v(17.1, 0) * mm});
            skPoint(sketch, "E227.orphan", {"position": v(0, 0) * mm});
            skLineSegment(sketch, "E228.trimOffspring", {"start": v(2.9, 0) * mm, "end": v(4.6, 0) * mm});
            skLineSegment(sketch, "E229.trimOffspring", {"start": v(5.4, 0) * mm, "end": v(7.1, 0) * mm});
            skLineSegment(sketch, "E230.trimOffspring", {"start": v(7.9, 0) * mm, "end": v(9.6, 0) * mm});
            skLineSegment(sketch, "E231.trimOffspring", {"start": v(10.4, 0) * mm, "end": v(12.1, 0) * mm});
            skLineSegment(sketch, "E232.trimOffspring", {"start": v(12.9, 0) * mm, "end": v(14.6, 0) * mm});
            skSolve(sketch);
        }
        {
            var Q0;
            Q0=qSketchRegion(id+"F0",true);
            extrude(context, id + "F1", {"entities" : qUnion([Q0]), "depth" : 2.5 * mm});
        }
    });
